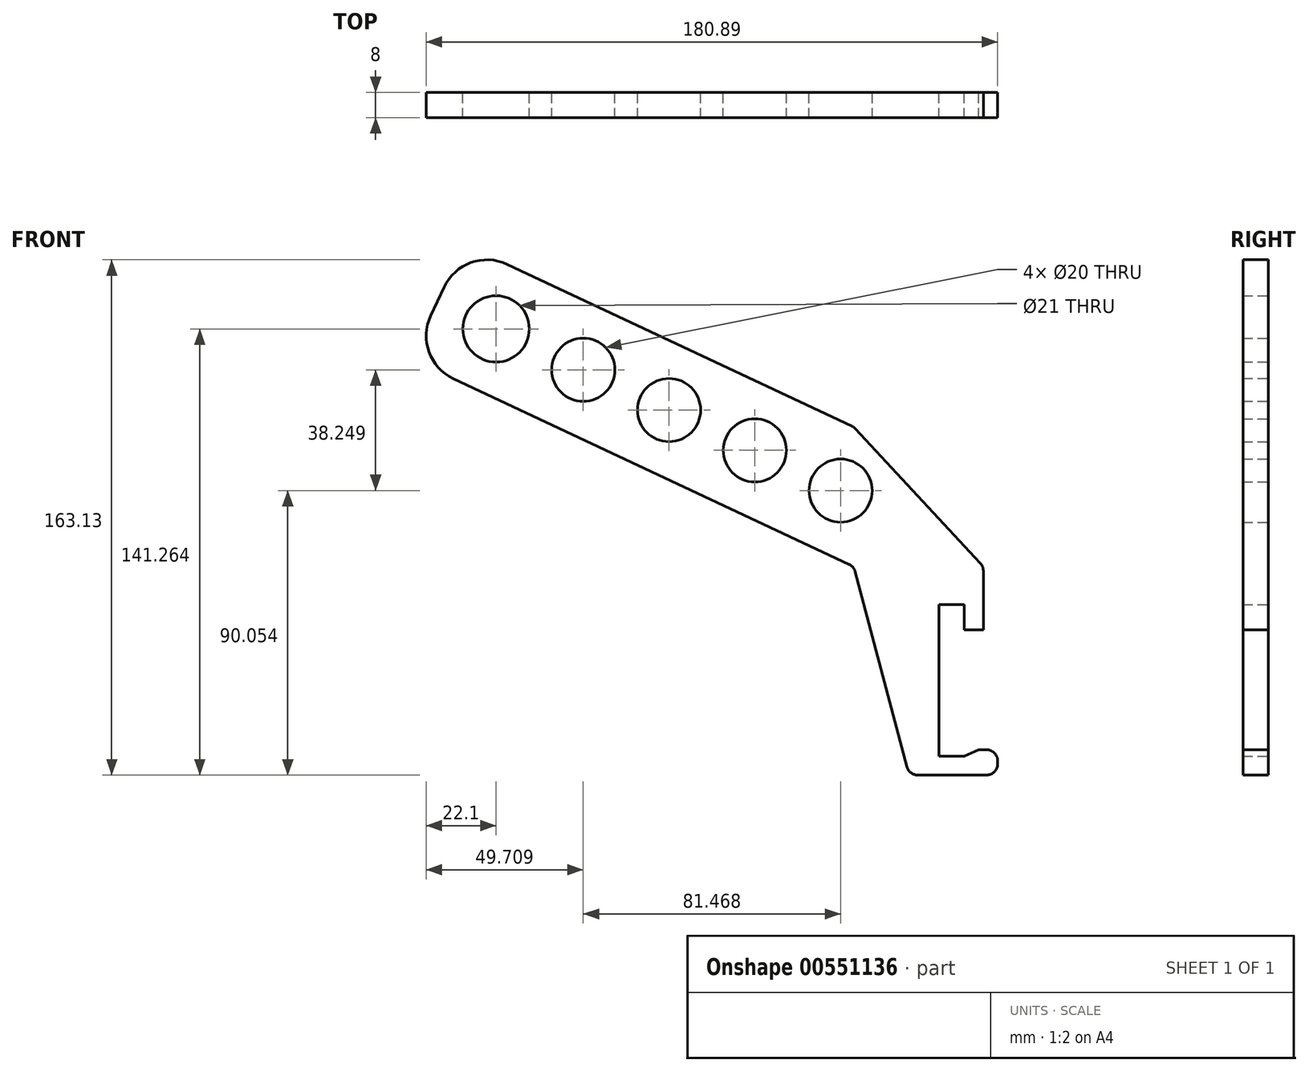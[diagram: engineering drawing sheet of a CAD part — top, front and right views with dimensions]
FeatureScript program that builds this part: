
annotation { "Feature Type Name" : "Feature", "Feature Type Description" : "" }
export const myFeature = defineFeature(function(context is Context, id is Id, definition is map)
    precondition{}
    {
        {
            var Q0;
            Q0=qCreatedBy(makeId("Front.planeOp"),FACE);
            var sketch = newSketch(context, id + "F0", { "sketchPlane" : qUnion([Q0])});
            skLineSegment(sketch, "E0", {"start": v(0, 0) * mm, "end": v(-140.3, 65.87) * mm});
            skLineSegment(sketch, "E1", {"start": v(-140.3, 65.87) * mm, "end": v(-123.3, 102.08) * mm});
            skLineSegment(sketch, "E2", {"start": v(-123.3, 102.08) * mm, "end": v(0, 44.19) * mm});
            skLineSegment(sketch, "E3", {"start": v(41, 0) * mm, "end": v(41, -20) * mm});
            skLineSegment(sketch, "E4", {"start": v(41, -20) * mm, "end": v(35, -20) * mm});
            skLineSegment(sketch, "E5", {"start": v(35, -20) * mm, "end": v(35, -12) * mm});
            skLineSegment(sketch, "E6", {"start": v(35, -12) * mm, "end": v(27, -12) * mm});
            skLineSegment(sketch, "E7", {"start": v(27, -12) * mm, "end": v(27, -60) * mm});
            skLineSegment(sketch, "E8", {"start": v(27, -60) * mm, "end": v(35, -60) * mm});
            skLineSegment(sketch, "E9", {"start": v(35, -60) * mm, "end": v(39.57, -58) * mm});
            skLineSegment(sketch, "E10", {"start": v(39.57, -58) * mm, "end": v(45.57, -58) * mm});
            skLineSegment(sketch, "E11", {"start": v(45.57, -58) * mm, "end": v(45.5, -66) * mm});
            skLineSegment(sketch, "E12", {"start": v(45.5, -66) * mm, "end": v(17.5, -66) * mm});
            skLineSegment(sketch, "E13", {"start": v(0, 0) * mm, "end": v(17.5, -66) * mm});
            skCircle(sketch, "E14", {"center": v(-113.25, 75.26) * mm, "radius": 10.5 * mm});
            skLineSegment(sketch, "E15", {"start": v(0, 44.19) * mm, "end": v(41, 0) * mm});
            skLineSegment(sketch, "E16", {"start": v(-131.8, 83.98) * mm, "end": v(9.54, 17.61) * mm, "construction": true});
            skCircle(sketch, "E17", {"center": v(-85.64, 62.3) * mm, "radius": 10 * mm});
            skCircle(sketch, "E18", {"center": v(-58.49, 49.55) * mm, "radius": 10 * mm});
            skCircle(sketch, "E19", {"center": v(-31.33, 36.8) * mm, "radius": 10 * mm});
            skCircle(sketch, "E20", {"center": v(-4.17, 24.05) * mm, "radius": 10 * mm});
            skSolve(sketch);
        }
        {
            var Q0;
            Q0=makeQuery(id+"F0.imprint","IMPRINT",FACE,{"disambiguationData":[TD([[makeQuery(id+"F0.imprint","IMPRINT",EDGE,{"derivedFrom":sQuery(id+"F0.wireOp",EDGE,"E0")}),-1.0]])]});
            extrude(context, id + "F1", {"entities" : qUnion([Q0]), "depth" : 8 * mm, "offsetDistance" : 25 * mm});
        }
        {
            var Q0;
            Q0=makeQuery(id+"F1.opExtrude","SWEPT_EDGE",EDGE,{"disambiguationData":[OSD([sQuery(id+"F0.wireOp",EDGE,"E1"),sQuery(id+"F0.wireOp",EDGE,"E2")])]});
            var Q1;
            Q1=makeQuery(id+"F1.opExtrude","SWEPT_EDGE",EDGE,{"disambiguationData":[OSD([sQuery(id+"F0.wireOp",EDGE,"E0"),sQuery(id+"F0.wireOp",EDGE,"E1")])]});
            fillet(context, id + "F2", {"entities" : qUnion([Q0, Q1]), "radius" : 15 * mm, "tangentPropagation" : true, "allowEdgeOverflow" : false});
        }
        {
            var Q0;
            Q0=makeQuery(id+"F1.opExtrude","SWEPT_EDGE",EDGE,{"disambiguationData":[OSD([sQuery(id+"F0.wireOp",EDGE,"E0"),sQuery(id+"F0.wireOp",EDGE,"E13")])]});
            var Q1;
            Q1=makeQuery(id+"F1.opExtrude","SWEPT_EDGE",EDGE,{"disambiguationData":[OSD([sQuery(id+"F0.wireOp",EDGE,"E3"),sQuery(id+"F0.wireOp",EDGE,"E15")])]});
            var Q2;
            Q2=makeQuery(id+"F1.opExtrude","SWEPT_EDGE",EDGE,{"disambiguationData":[OSD([sQuery(id+"F0.wireOp",EDGE,"E2"),sQuery(id+"F0.wireOp",EDGE,"E15")])]});
            var Q3;
            Q3=makeQuery(id+"F1.opExtrude","SWEPT_EDGE",EDGE,{"disambiguationData":[OSD([sQuery(id+"F0.wireOp",EDGE,"E10"),sQuery(id+"F0.wireOp",EDGE,"E11")])]});
            var Q4;
            Q4=makeQuery(id+"F1.opExtrude","SWEPT_EDGE",EDGE,{"disambiguationData":[OSD([sQuery(id+"F0.wireOp",EDGE,"E11"),sQuery(id+"F0.wireOp",EDGE,"E12")])]});
            var Q5;
            Q5=makeQuery(id+"F1.opExtrude","SWEPT_EDGE",EDGE,{"disambiguationData":[OSD([sQuery(id+"F0.wireOp",EDGE,"E12"),sQuery(id+"F0.wireOp",EDGE,"E13")])]});
            fillet(context, id + "F3", {"entities" : qUnion([Q0, Q1, Q2, Q3, Q4, Q5]), "radius" : 3.5 * mm, "tangentPropagation" : true, "allowEdgeOverflow" : false});
        }
    });
